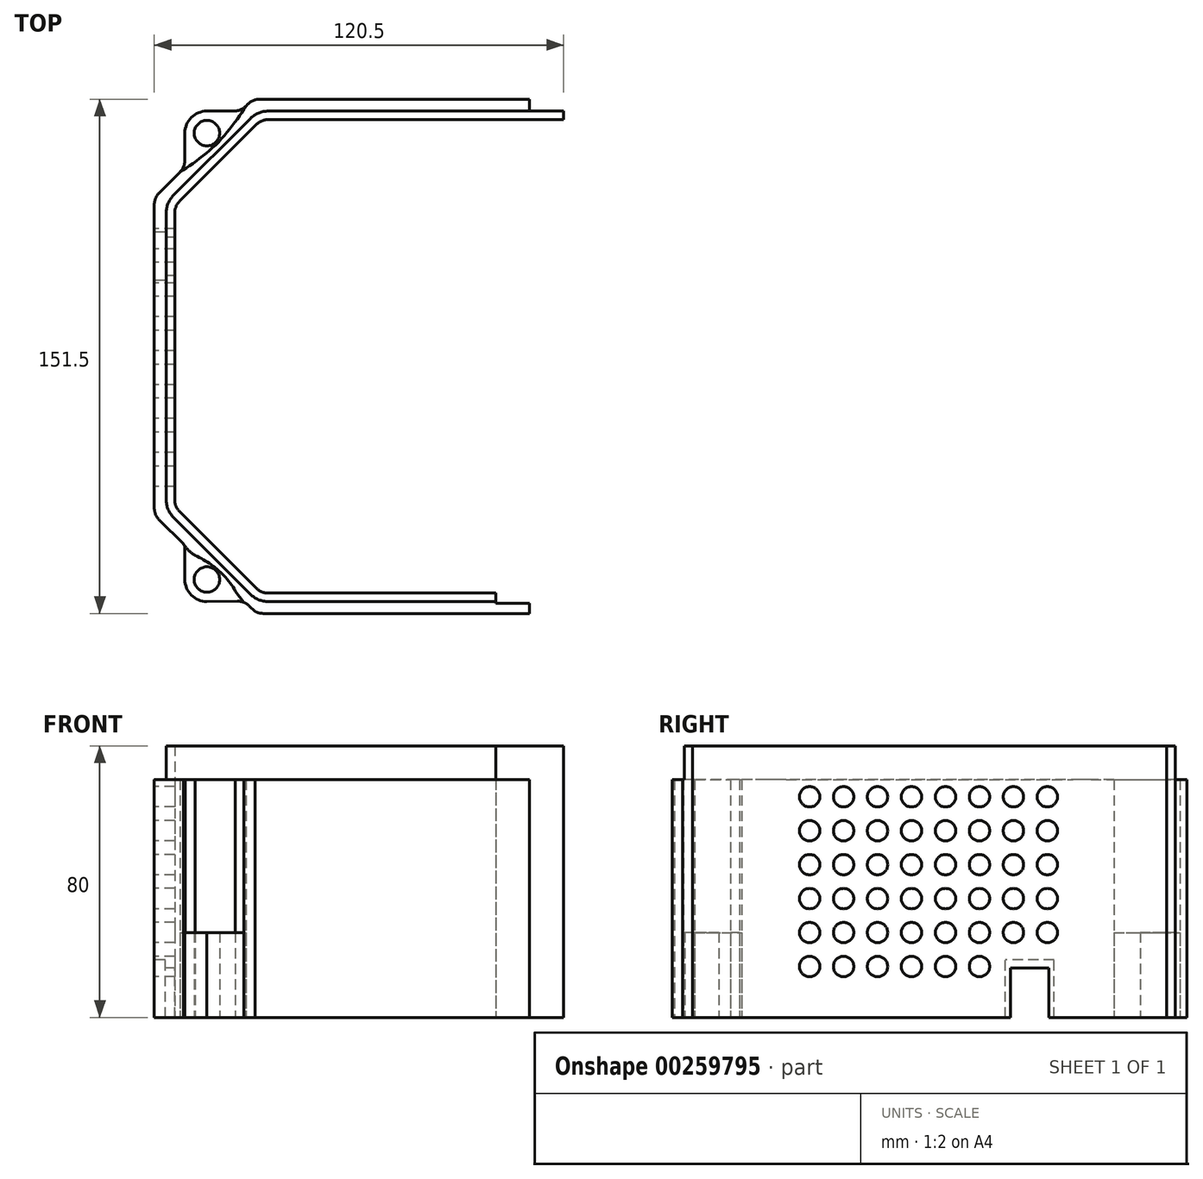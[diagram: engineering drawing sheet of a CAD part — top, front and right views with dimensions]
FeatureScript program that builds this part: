
annotation { "Feature Type Name" : "Feature", "Feature Type Description" : "" }
export const myFeature = defineFeature(function(context is Context, id is Id, definition is map)
    precondition{}
    {
        {
            var Q0;
            Q0=qCreatedBy(makeId("Top.planeOp"),FACE);
            var sketch = newSketch(context, id + "F0", { "sketchPlane" : qUnion([Q0])});
            skLineSegment(sketch, "E0.bottom", {"start": v(-49.42, 75.75) * mm, "end": v(30, 75.75) * mm});
            skLineSegment(sketch, "E0.top", {"start": v(-48.4, -75.75) * mm, "end": v(30, -75.75) * mm});
            skLineSegment(sketch, "E0.left", {"start": v(-80.5, 44.67) * mm, "end": v(-80.5, -44.67) * mm});
            skLineSegment(sketch, "E0.right", {"start": v(30, 75.75) * mm, "end": v(30, 72.25) * mm});
            skCircle(sketch, "E1", {"center": v(-65, 65.75) * mm, "radius": 3.75 * mm});
            skCircle(sketch, "E2", {"center": v(-65, -65.75) * mm, "radius": 3.75 * mm});
            skPoint(sketch, "E3.visualSharp", {"position": v(-80.5, 75.75) * mm});
            skPoint(sketch, "E4.visualSharp", {"position": v(-80.5, -75.75) * mm});
            skLineSegment(sketch, "E5.0", {"start": v(-46.93, 69.75) * mm, "end": v(30, 69.75) * mm});
            skLineSegment(sketch, "E6.trimOffspring", {"start": v(30, -72.75) * mm, "end": v(30, -75.75) * mm});
            skLineSegment(sketch, "E7", {"start": v(-73.04, 45.72) * mm, "end": v(-50.47, 68.29) * mm});
            skLineSegment(sketch, "E8", {"start": v(-73.04, -45.72) * mm, "end": v(-50.47, -68.29) * mm});
            skLineSegment(sketch, "E9.trimOffspring", {"start": v(-46.94, -69.75) * mm, "end": v(20, -69.75) * mm});
            skArc(sketch, "E10.trimOffspring", {"start": v(-60.05, -58.7) * mm, "mid": v(-60.25, -58.5) * mm, "end": v(-60.46, -58.3) * mm, "construction": true});
            skArc(sketch, "E11", {"start": v(-71.5, -65.75) * mm, "mid": v(-69.6, -70.35) * mm, "end": v(-65, -72.25) * mm});
            skArc(sketch, "E12", {"start": v(-65, 72.25) * mm, "mid": v(-69.6, 70.35) * mm, "end": v(-71.5, 65.75) * mm});
            skPoint(sketch, "E13.visualSharp", {"position": v(-49, -69.75) * mm});
            skArc(sketch, "E13.filletArc", {"start": v(-50.47, -68.29) * mm, "mid": v(-48.85, -69.37) * mm, "end": v(-46.94, -69.75) * mm});
            skPoint(sketch, "E14.visualSharp", {"position": v(-74.5, -44.26) * mm});
            skArc(sketch, "E14.filletArc", {"start": v(-74.5, -42.19) * mm, "mid": v(-74.12, -44.1) * mm, "end": v(-73.04, -45.72) * mm});
            skPoint(sketch, "E15.visualSharp", {"position": v(-74.5, 44.25) * mm});
            skArc(sketch, "E15.filletArc", {"start": v(-73.04, 45.72) * mm, "mid": v(-74.12, 44.1) * mm, "end": v(-74.5, 42.18) * mm});
            skPoint(sketch, "E16.visualSharp", {"position": v(-49, 69.75) * mm});
            skArc(sketch, "E16.filletArc", {"start": v(-46.93, 69.75) * mm, "mid": v(-48.85, 69.37) * mm, "end": v(-50.47, 68.29) * mm});
            skLineSegment(sketch, "E17", {"start": v(-79.04, -48.2) * mm, "end": v(-71.96, -55.28) * mm});
            skPoint(sketch, "E18.visualSharp", {"position": v(-70.5, -56.75) * mm});
            skArc(sketch, "E19.filletArc", {"start": v(-80.5, -44.67) * mm, "mid": v(-80.12, -46.59) * mm, "end": v(-79.04, -48.2) * mm});
            skPoint(sketch, "E20.visualSharp", {"position": v(-56, -71.25) * mm});
            skPoint(sketch, "E21.visualSharp", {"position": v(-51.5, -75.75) * mm});
            skArc(sketch, "E21.filletArc", {"start": v(-50.86, -75.1) * mm, "mid": v(-49.68, -75.59) * mm, "end": v(-48.4, -75.75) * mm});
            skLineSegment(sketch, "E22", {"start": v(-65, 72.25) * mm, "end": v(-57.06, 72.25) * mm});
            skLineSegment(sketch, "E23", {"start": v(-71.5, 57.81) * mm, "end": v(-71.5, 65.75) * mm});
            skLineSegment(sketch, "E24", {"start": v(-72.96, 54.28) * mm, "end": v(-79.04, 48.2) * mm});
            skLineSegment(sketch, "E25", {"start": v(-53.53, 73.71) * mm, "end": v(-52.95, 74.29) * mm});
            skPoint(sketch, "E26.visualSharp", {"position": v(-80.5, 46.74) * mm});
            skArc(sketch, "E26.filletArc", {"start": v(-79.04, 48.2) * mm, "mid": v(-80.12, 46.58) * mm, "end": v(-80.5, 44.67) * mm});
            skPoint(sketch, "E27.visualSharp", {"position": v(-71.5, 55.74) * mm});
            skArc(sketch, "E27.filletArc", {"start": v(-72.96, 54.28) * mm, "mid": v(-71.88, 55.9) * mm, "end": v(-71.5, 57.81) * mm});
            skPoint(sketch, "E28.visualSharp", {"position": v(-54.99, 72.25) * mm});
            skArc(sketch, "E28.filletArc", {"start": v(-57.06, 72.25) * mm, "mid": v(-55.15, 72.63) * mm, "end": v(-53.53, 73.71) * mm});
            skPoint(sketch, "E29.visualSharp", {"position": v(-51.49, 75.75) * mm});
            skArc(sketch, "E29.filletArc", {"start": v(-49.42, 75.75) * mm, "mid": v(-51.33, 75.37) * mm, "end": v(-52.95, 74.29) * mm});
            skLineSegment(sketch, "E30", {"start": v(-74.5, -42.19) * mm, "end": v(-74.5, 42.18) * mm});
            skLineSegment(sketch, "E31", {"start": v(-59, -59.75) * mm, "end": v(-80.03, -80.78) * mm, "construction": true});
            skArc(sketch, "E32.filletArc", {"start": v(-71.36, -56.02) * mm, "mid": v(-70.06, -57.5) * mm, "end": v(-68.44, -58.62) * mm});
            skPoint(sketch, "E33.orphan", {"position": v(-62.35, -63.1) * mm});
            skPoint(sketch, "E34.orphan", {"position": v(-56, -69.45) * mm});
            skPoint(sketch, "E35.orphan", {"position": v(-68.7, -56.75) * mm});
            skPoint(sketch, "E36", {"position": v(-62, -62.74) * mm});
            skFitSpline(sketch, "E37", {"points": [v(-56.66, -69.17) * mm, v(-62, -62.74) * mm, v(-68.44, -58.62) * mm], "startDerivative": vector(-7.08, 14.05) * mm, "endDerivative": vector(-14.05, 7.08) * mm});
            skLineSegment(sketch, "E38", {"start": v(-62, 62.74) * mm, "end": v(-62.35, 63.1) * mm, "construction": true});
            skPoint(sketch, "E39", {"position": v(-62, 62.74) * mm});
            skFitSpline(sketch, "E40", {"points": [v(-72.96, 54.28) * mm, v(-62, 62.74) * mm, v(-53.53, 73.71) * mm], "startDerivative": vector(21.19, 13.69) * mm, "endDerivative": vector(13.69, 21.19) * mm});
            skLineSegment(sketch, "E41.trimOffspring", {"start": v(-67.65, 68.4) * mm, "end": v(-69.6, 70.35) * mm, "construction": true});
            skLineSegment(sketch, "E42", {"start": v(-71.97, -55.28) * mm, "end": v(-71.96, -55.28) * mm});
            skLineSegment(sketch, "E43", {"start": v(-71.5, -65.75) * mm, "end": v(-71.5, -56.56) * mm});
            skLineSegment(sketch, "E44", {"start": v(-65, -72.25) * mm, "end": v(-56.04, -72.14) * mm});
            skArc(sketch, "E45.filletArc", {"start": v(-71.5, -56.56) * mm, "mid": v(-71.62, -55.88) * mm, "end": v(-71.97, -55.28) * mm});
            skLineSegment(sketch, "E46", {"start": v(-50.86, -75.1) * mm, "end": v(-52.55, -73.51) * mm});
            skPoint(sketch, "E47.visualSharp", {"position": v(-54.02, -72.12) * mm});
            skArc(sketch, "E47.filletArc", {"start": v(-52.55, -73.51) * mm, "mid": v(-54.16, -72.49) * mm, "end": v(-56.04, -72.14) * mm});
            skLineSegment(sketch, "E48", {"start": v(-56.66, -69.17) * mm, "end": v(-54.16, -72.49) * mm});
            skLineSegment(sketch, "E49", {"start": v(-71.36, -56.02) * mm, "end": v(-71.96, -55.28) * mm});
            skLineSegment(sketch, "E50.bottom", {"start": v(30, 69.75) * mm, "end": v(40, 69.75) * mm});
            skLineSegment(sketch, "E50.top", {"start": v(30, 72.25) * mm, "end": v(40, 72.25) * mm});
            skLineSegment(sketch, "E50.right", {"start": v(40, 69.75) * mm, "end": v(40, 72.25) * mm});
            skLineSegment(sketch, "E51.top", {"start": v(20, -72.75) * mm, "end": v(30, -72.75) * mm});
            skLineSegment(sketch, "E51.left", {"start": v(20, -69.75) * mm, "end": v(20, -72.75) * mm});
            skSolve(sketch);
        }
        {
            var Q0;
            Q0=makeQuery(id+"F0.imprint","IMPRINT",FACE,{"disambiguationData":[TD([[makeQuery(id+"F0.imprint","IMPRINT",EDGE,{"derivedFrom":sQuery(id+"F0.wireOp",EDGE,"E2")}),-1.0]])]});
            var Q1;
            Q1=makeQuery(id+"F0.imprint","IMPRINT",FACE,{"disambiguationData":[TD([[makeQuery(id+"F0.imprint","IMPRINT",EDGE,{"derivedFrom":sQuery(id+"F0.wireOp",EDGE,"E1")}),-1.0]])]});
            extrude(context, id + "F1", {"entities" : qUnion([Q0, Q1]), "depth" : 25 * mm});
        }
        {
            var Q0;
            Q0=makeQuery(id+"F0.imprint","IMPRINT",FACE,{"disambiguationData":[TD([[makeQuery(id+"F0.imprint","IMPRINT",EDGE,{"derivedFrom":sQuery(id+"F0.wireOp",EDGE,"E0.bottom")}),-1.0]])]});
            extrude(context, id + "F2", {"entities" : qUnion([Q0]), "depth" : 70 * mm});
        }
        {
            var Q0;
            Q0=makeQuery(id+"F2.opExtrude","CAP_FACE",FACE,{"disambiguationData":[OSD([sQuery(id+"F0.wireOp",EDGE,"E0.bottom"),sQuery(id+"F0.wireOp",EDGE,"E0.top"),sQuery(id+"F0.wireOp",EDGE,"E0.left"),sQuery(id+"F0.wireOp",EDGE,"E0.right"),sQuery(id+"F0.wireOp",EDGE,"E5.0"),sQuery(id+"F0.wireOp",EDGE,"E6.trimOffspring"),sQuery(id+"F0.wireOp",EDGE,"E7"),sQuery(id+"F0.wireOp",EDGE,"E8"),sQuery(id+"F0.wireOp",EDGE,"E9.trimOffspring"),sQuery(id+"F0.wireOp",EDGE,"E13.filletArc"),sQuery(id+"F0.wireOp",EDGE,"E14.filletArc"),sQuery(id+"F0.wireOp",EDGE,"E15.filletArc"),sQuery(id+"F0.wireOp",EDGE,"E16.filletArc"),sQuery(id+"F0.wireOp",EDGE,"E17"),sQuery(id+"F0.wireOp",EDGE,"E19.filletArc"),sQuery(id+"F0.wireOp",EDGE,"E21.filletArc"),sQuery(id+"F0.wireOp",EDGE,"E24"),sQuery(id+"F0.wireOp",EDGE,"E25"),sQuery(id+"F0.wireOp",EDGE,"E26.filletArc"),sQuery(id+"F0.wireOp",EDGE,"E29.filletArc"),sQuery(id+"F0.wireOp",EDGE,"E30"),sQuery(id+"F0.wireOp",EDGE,"E32.filletArc"),sQuery(id+"F0.wireOp",EDGE,"E37"),sQuery(id+"F0.wireOp",EDGE,"E40"),sQuery(id+"F0.wireOp",EDGE,"E46"),sQuery(id+"F0.wireOp",EDGE,"E47.filletArc"),sQuery(id+"F0.wireOp",EDGE,"E48"),sQuery(id+"F0.wireOp",EDGE,"E49"),sQuery(id+"F0.wireOp",EDGE,"E50.bottom"),sQuery(id+"F0.wireOp",EDGE,"E50.top"),sQuery(id+"F0.wireOp",EDGE,"E50.right"),sQuery(id+"F0.wireOp",EDGE,"E51.top"),sQuery(id+"F0.wireOp",EDGE,"E51.left")])],"isStart":false});
            var sketch = newSketch(context, id + "F3", { "sketchPlane" : qUnion([Q0])});
            skLineSegment(sketch, "E52.0", {"start": v(-46.94, -72.25) * mm, "end": v(20, -72.25) * mm});
            skArc(sketch, "E52.1", {"start": v(-52.24, -70.05) * mm, "mid": v(-49.8, -71.68) * mm, "end": v(-46.94, -72.25) * mm});
            skLineSegment(sketch, "E52.2", {"start": v(-74.8, -47.5) * mm, "end": v(-52.24, -70.05) * mm});
            skArc(sketch, "E52.3", {"start": v(-77, -42.19) * mm, "mid": v(-76.43, -45.06) * mm, "end": v(-74.8, -47.5) * mm});
            skLineSegment(sketch, "E52.4", {"start": v(-77, -42.19) * mm, "end": v(-77, 42.18) * mm});
            skArc(sketch, "E52.5", {"start": v(-74.8, 47.49) * mm, "mid": v(-76.43, 45.05) * mm, "end": v(-77, 42.18) * mm});
            skLineSegment(sketch, "E52.6", {"start": v(30, 72.25) * mm, "end": v(40, 72.25) * mm});
            skLineSegment(sketch, "E52.7", {"start": v(-46.93, 72.25) * mm, "end": v(30, 72.25) * mm});
            skArc(sketch, "E52.8", {"start": v(-46.93, 72.25) * mm, "mid": v(-49.8, 71.68) * mm, "end": v(-52.24, 70.05) * mm});
            skLineSegment(sketch, "E52.9", {"start": v(-74.8, 47.49) * mm, "end": v(-52.24, 70.05) * mm});
            skLineSegment(sketch, "E53", {"start": v(20, -72.25) * mm, "end": v(20, -69.75) * mm});
            skLineSegment(sketch, "E54", {"start": v(40, 69.75) * mm, "end": v(40, 72.25) * mm});
            skSolve(sketch);
        }
        {
            var Q0;
            Q0=makeQuery(id+"F3.imprint","IMPRINT",FACE,{"disambiguationData":[TD([[makeQuery(id+"F3.imprint","IMPRINT",EDGE,{"derivedFrom":sQuery(id+"F3.wireOp",EDGE,"E52.0")}),1.0]])]});
            extrude(context, id + "F4", {"entities" : qUnion([Q0]), "operationType" : NewBodyOperationType.ADD, "depth" : 10 * mm});
        }
        {
            var Q0;
            Q0=makeQuery(id+"F2.opExtrude","SWEPT_FACE",FACE,{"disambiguationData":[OSD([sQuery(id+"F0.wireOp",EDGE,"E0.left")])]});
            var sketch = newSketch(context, id + "F5", { "sketchPlane" : qUnion([Q0])});
            skCircle(sketch, "E55.0.1.0", {"center": v(-34.67, 25) * mm, "radius": 3 * mm});
            skCircle(sketch, "E55.0.2.0", {"center": v(-34.67, 35) * mm, "radius": 3 * mm});
            skCircle(sketch, "E55.0.3.0", {"center": v(-34.67, 45) * mm, "radius": 3 * mm});
            skCircle(sketch, "E55.0.4.0", {"center": v(-34.67, 55) * mm, "radius": 3 * mm});
            skCircle(sketch, "E55.0.5.0", {"center": v(-34.67, 65) * mm, "radius": 3 * mm});
            skCircle(sketch, "E55.1.1.0", {"center": v(-24.67, 25) * mm, "radius": 3 * mm});
            skCircle(sketch, "E55.1.2.0", {"center": v(-24.67, 35) * mm, "radius": 3 * mm});
            skCircle(sketch, "E55.1.3.0", {"center": v(-24.67, 45) * mm, "radius": 3 * mm});
            skCircle(sketch, "E55.1.4.0", {"center": v(-24.67, 55) * mm, "radius": 3 * mm});
            skCircle(sketch, "E55.1.5.0", {"center": v(-24.67, 65) * mm, "radius": 3 * mm});
            skCircle(sketch, "E55.2.0.0", {"center": v(-14.67, 15) * mm, "radius": 3 * mm});
            skCircle(sketch, "E55.2.1.0", {"center": v(-14.67, 25) * mm, "radius": 3 * mm});
            skCircle(sketch, "E55.2.2.0", {"center": v(-14.67, 35) * mm, "radius": 3 * mm});
            skCircle(sketch, "E55.2.3.0", {"center": v(-14.67, 45) * mm, "radius": 3 * mm});
            skCircle(sketch, "E55.2.4.0", {"center": v(-14.67, 55) * mm, "radius": 3 * mm});
            skCircle(sketch, "E55.2.5.0", {"center": v(-14.67, 65) * mm, "radius": 3 * mm});
            skCircle(sketch, "E55.3.0.0", {"center": v(-4.67, 15) * mm, "radius": 3 * mm});
            skCircle(sketch, "E55.3.1.0", {"center": v(-4.67, 25) * mm, "radius": 3 * mm});
            skCircle(sketch, "E55.3.2.0", {"center": v(-4.67, 35) * mm, "radius": 3 * mm});
            skCircle(sketch, "E55.3.3.0", {"center": v(-4.67, 45) * mm, "radius": 3 * mm});
            skCircle(sketch, "E55.3.4.0", {"center": v(-4.67, 55) * mm, "radius": 3 * mm});
            skCircle(sketch, "E55.3.5.0", {"center": v(-4.67, 65) * mm, "radius": 3 * mm});
            skCircle(sketch, "E55.4.0.0", {"center": v(5.33, 15) * mm, "radius": 3 * mm});
            skCircle(sketch, "E55.4.1.0", {"center": v(5.33, 25) * mm, "radius": 3 * mm});
            skCircle(sketch, "E55.4.2.0", {"center": v(5.33, 35) * mm, "radius": 3 * mm});
            skCircle(sketch, "E55.4.3.0", {"center": v(5.33, 45) * mm, "radius": 3 * mm});
            skCircle(sketch, "E55.4.4.0", {"center": v(5.33, 55) * mm, "radius": 3 * mm});
            skCircle(sketch, "E55.4.5.0", {"center": v(5.33, 65) * mm, "radius": 3 * mm});
            skCircle(sketch, "E55.5.0.0", {"center": v(15.33, 15) * mm, "radius": 3 * mm});
            skCircle(sketch, "E55.5.1.0", {"center": v(15.33, 25) * mm, "radius": 3 * mm});
            skCircle(sketch, "E55.5.2.0", {"center": v(15.33, 35) * mm, "radius": 3 * mm});
            skCircle(sketch, "E55.5.3.0", {"center": v(15.33, 45) * mm, "radius": 3 * mm});
            skCircle(sketch, "E55.5.4.0", {"center": v(15.33, 55) * mm, "radius": 3 * mm});
            skCircle(sketch, "E55.5.5.0", {"center": v(15.33, 65) * mm, "radius": 3 * mm});
            skCircle(sketch, "E55.6.0.0", {"center": v(25.33, 15) * mm, "radius": 3 * mm});
            skCircle(sketch, "E55.6.1.0", {"center": v(25.33, 25) * mm, "radius": 3 * mm});
            skCircle(sketch, "E55.6.2.0", {"center": v(25.33, 35) * mm, "radius": 3 * mm});
            skCircle(sketch, "E55.6.3.0", {"center": v(25.33, 45) * mm, "radius": 3 * mm});
            skCircle(sketch, "E55.6.4.0", {"center": v(25.33, 55) * mm, "radius": 3 * mm});
            skCircle(sketch, "E55.6.5.0", {"center": v(25.33, 65) * mm, "radius": 3 * mm});
            skCircle(sketch, "E55.7.0.0", {"center": v(35.33, 15) * mm, "radius": 3 * mm});
            skCircle(sketch, "E55.7.1.0", {"center": v(35.33, 25) * mm, "radius": 3 * mm});
            skCircle(sketch, "E55.7.2.0", {"center": v(35.33, 35) * mm, "radius": 3 * mm});
            skCircle(sketch, "E55.7.3.0", {"center": v(35.33, 45) * mm, "radius": 3 * mm});
            skCircle(sketch, "E55.7.4.0", {"center": v(35.33, 55) * mm, "radius": 3 * mm});
            skCircle(sketch, "E55.7.5.0", {"center": v(35.33, 65) * mm, "radius": 3 * mm});
            skLineSegment(sketch, "E55.direction1", {"start": v(-34.67, 15) * mm, "end": v(-24.67, 15) * mm, "construction": true});
            skLineSegment(sketch, "E55.direction2", {"start": v(-34.67, 15) * mm, "end": v(-34.67, 25) * mm, "construction": true});
            skSolve(sketch);
        }
        {
            var Q0;
            Q0=makeQuery(id+"F5.imprint","IMPRINT",FACE,{"disambiguationData":[TD([[makeQuery(id+"F5.imprint","IMPRINT",EDGE,{"derivedFrom":sQuery(id+"F5.wireOp",EDGE,"E55.1.5.0")}),1.0]])]});
            var Q1;
            Q1=makeQuery(id+"F5.imprint","IMPRINT",FACE,{"disambiguationData":[TD([[makeQuery(id+"F5.imprint","IMPRINT",EDGE,{"derivedFrom":sQuery(id+"F5.wireOp",EDGE,"E55.0.5.0")}),1.0]])]});
            var Q2;
            Q2=makeQuery(id+"F5.imprint","IMPRINT",FACE,{"disambiguationData":[TD([[makeQuery(id+"F5.imprint","IMPRINT",EDGE,{"derivedFrom":sQuery(id+"F5.wireOp",EDGE,"E55.2.5.0")}),1.0]])]});
            var Q3;
            Q3=makeQuery(id+"F5.imprint","IMPRINT",FACE,{"disambiguationData":[TD([[makeQuery(id+"F5.imprint","IMPRINT",EDGE,{"derivedFrom":sQuery(id+"F5.wireOp",EDGE,"E55.3.5.0")}),1.0]])]});
            var Q4;
            Q4=makeQuery(id+"F5.imprint","IMPRINT",FACE,{"disambiguationData":[TD([[makeQuery(id+"F5.imprint","IMPRINT",EDGE,{"derivedFrom":sQuery(id+"F5.wireOp",EDGE,"E55.4.5.0")}),1.0]])]});
            var Q5;
            Q5=makeQuery(id+"F5.imprint","IMPRINT",FACE,{"disambiguationData":[TD([[makeQuery(id+"F5.imprint","IMPRINT",EDGE,{"derivedFrom":sQuery(id+"F5.wireOp",EDGE,"E55.5.5.0")}),1.0]])]});
            var Q6;
            Q6=makeQuery(id+"F5.imprint","IMPRINT",FACE,{"disambiguationData":[TD([[makeQuery(id+"F5.imprint","IMPRINT",EDGE,{"derivedFrom":sQuery(id+"F5.wireOp",EDGE,"E55.6.5.0")}),1.0]])]});
            var Q7;
            Q7=makeQuery(id+"F5.imprint","IMPRINT",FACE,{"disambiguationData":[TD([[makeQuery(id+"F5.imprint","IMPRINT",EDGE,{"derivedFrom":sQuery(id+"F5.wireOp",EDGE,"E55.7.5.0")}),1.0]])]});
            var Q8;
            Q8=makeQuery(id+"F5.imprint","IMPRINT",FACE,{"disambiguationData":[TD([[makeQuery(id+"F5.imprint","IMPRINT",EDGE,{"derivedFrom":sQuery(id+"F5.wireOp",EDGE,"E55.7.4.0")}),1.0]])]});
            var Q9;
            Q9=makeQuery(id+"F5.imprint","IMPRINT",FACE,{"disambiguationData":[TD([[makeQuery(id+"F5.imprint","IMPRINT",EDGE,{"derivedFrom":sQuery(id+"F5.wireOp",EDGE,"E55.6.4.0")}),1.0]])]});
            var Q10;
            Q10=makeQuery(id+"F5.imprint","IMPRINT",FACE,{"disambiguationData":[TD([[makeQuery(id+"F5.imprint","IMPRINT",EDGE,{"derivedFrom":sQuery(id+"F5.wireOp",EDGE,"E55.5.4.0")}),1.0]])]});
            var Q11;
            Q11=makeQuery(id+"F5.imprint","IMPRINT",FACE,{"disambiguationData":[TD([[makeQuery(id+"F5.imprint","IMPRINT",EDGE,{"derivedFrom":sQuery(id+"F5.wireOp",EDGE,"E55.4.4.0")}),1.0]])]});
            var Q12;
            Q12=makeQuery(id+"F5.imprint","IMPRINT",FACE,{"disambiguationData":[TD([[makeQuery(id+"F5.imprint","IMPRINT",EDGE,{"derivedFrom":sQuery(id+"F5.wireOp",EDGE,"E55.3.4.0")}),1.0]])]});
            var Q13;
            Q13=makeQuery(id+"F5.imprint","IMPRINT",FACE,{"disambiguationData":[TD([[makeQuery(id+"F5.imprint","IMPRINT",EDGE,{"derivedFrom":sQuery(id+"F5.wireOp",EDGE,"E55.2.4.0")}),1.0]])]});
            var Q14;
            Q14=makeQuery(id+"F5.imprint","IMPRINT",FACE,{"disambiguationData":[TD([[makeQuery(id+"F5.imprint","IMPRINT",EDGE,{"derivedFrom":sQuery(id+"F5.wireOp",EDGE,"E55.1.4.0")}),1.0]])]});
            var Q15;
            Q15=makeQuery(id+"F5.imprint","IMPRINT",FACE,{"disambiguationData":[TD([[makeQuery(id+"F5.imprint","IMPRINT",EDGE,{"derivedFrom":sQuery(id+"F5.wireOp",EDGE,"E55.0.4.0")}),1.0]])]});
            var Q16;
            Q16=makeQuery(id+"F5.imprint","IMPRINT",FACE,{"disambiguationData":[TD([[makeQuery(id+"F5.imprint","IMPRINT",EDGE,{"derivedFrom":sQuery(id+"F5.wireOp",EDGE,"E55.0.3.0")}),1.0]])]});
            var Q17;
            Q17=makeQuery(id+"F5.imprint","IMPRINT",FACE,{"disambiguationData":[TD([[makeQuery(id+"F5.imprint","IMPRINT",EDGE,{"derivedFrom":sQuery(id+"F5.wireOp",EDGE,"E55.1.3.0")}),1.0]])]});
            var Q18;
            Q18=makeQuery(id+"F5.imprint","IMPRINT",FACE,{"disambiguationData":[TD([[makeQuery(id+"F5.imprint","IMPRINT",EDGE,{"derivedFrom":sQuery(id+"F5.wireOp",EDGE,"E55.2.3.0")}),1.0]])]});
            var Q19;
            Q19=makeQuery(id+"F5.imprint","IMPRINT",FACE,{"disambiguationData":[TD([[makeQuery(id+"F5.imprint","IMPRINT",EDGE,{"derivedFrom":sQuery(id+"F5.wireOp",EDGE,"E55.3.3.0")}),1.0]])]});
            var Q20;
            Q20=makeQuery(id+"F5.imprint","IMPRINT",FACE,{"disambiguationData":[TD([[makeQuery(id+"F5.imprint","IMPRINT",EDGE,{"derivedFrom":sQuery(id+"F5.wireOp",EDGE,"E55.4.3.0")}),1.0]])]});
            var Q21;
            Q21=makeQuery(id+"F5.imprint","IMPRINT",FACE,{"disambiguationData":[TD([[makeQuery(id+"F5.imprint","IMPRINT",EDGE,{"derivedFrom":sQuery(id+"F5.wireOp",EDGE,"E55.5.3.0")}),1.0]])]});
            var Q22;
            Q22=makeQuery(id+"F5.imprint","IMPRINT",FACE,{"disambiguationData":[TD([[makeQuery(id+"F5.imprint","IMPRINT",EDGE,{"derivedFrom":sQuery(id+"F5.wireOp",EDGE,"E55.6.3.0")}),1.0]])]});
            var Q23;
            Q23=makeQuery(id+"F5.imprint","IMPRINT",FACE,{"disambiguationData":[TD([[makeQuery(id+"F5.imprint","IMPRINT",EDGE,{"derivedFrom":sQuery(id+"F5.wireOp",EDGE,"E55.7.3.0")}),1.0]])]});
            var Q24;
            Q24=makeQuery(id+"F5.imprint","IMPRINT",FACE,{"disambiguationData":[TD([[makeQuery(id+"F5.imprint","IMPRINT",EDGE,{"derivedFrom":sQuery(id+"F5.wireOp",EDGE,"E55.7.2.0")}),1.0]])]});
            var Q25;
            Q25=makeQuery(id+"F5.imprint","IMPRINT",FACE,{"disambiguationData":[TD([[makeQuery(id+"F5.imprint","IMPRINT",EDGE,{"derivedFrom":sQuery(id+"F5.wireOp",EDGE,"E55.6.2.0")}),1.0]])]});
            var Q26;
            Q26=makeQuery(id+"F5.imprint","IMPRINT",FACE,{"disambiguationData":[TD([[makeQuery(id+"F5.imprint","IMPRINT",EDGE,{"derivedFrom":sQuery(id+"F5.wireOp",EDGE,"E55.5.2.0")}),1.0]])]});
            var Q27;
            Q27=makeQuery(id+"F5.imprint","IMPRINT",FACE,{"disambiguationData":[TD([[makeQuery(id+"F5.imprint","IMPRINT",EDGE,{"derivedFrom":sQuery(id+"F5.wireOp",EDGE,"E55.4.2.0")}),1.0]])]});
            var Q28;
            Q28=makeQuery(id+"F5.imprint","IMPRINT",FACE,{"disambiguationData":[TD([[makeQuery(id+"F5.imprint","IMPRINT",EDGE,{"derivedFrom":sQuery(id+"F5.wireOp",EDGE,"E55.3.2.0")}),1.0]])]});
            var Q29;
            Q29=makeQuery(id+"F5.imprint","IMPRINT",FACE,{"disambiguationData":[TD([[makeQuery(id+"F5.imprint","IMPRINT",EDGE,{"derivedFrom":sQuery(id+"F5.wireOp",EDGE,"E55.2.2.0")}),1.0]])]});
            var Q30;
            Q30=makeQuery(id+"F5.imprint","IMPRINT",FACE,{"disambiguationData":[TD([[makeQuery(id+"F5.imprint","IMPRINT",EDGE,{"derivedFrom":sQuery(id+"F5.wireOp",EDGE,"E55.1.2.0")}),1.0]])]});
            var Q31;
            Q31=makeQuery(id+"F5.imprint","IMPRINT",FACE,{"disambiguationData":[TD([[makeQuery(id+"F5.imprint","IMPRINT",EDGE,{"derivedFrom":sQuery(id+"F5.wireOp",EDGE,"E55.0.2.0")}),1.0]])]});
            var Q32;
            Q32=makeQuery(id+"F5.imprint","IMPRINT",FACE,{"disambiguationData":[TD([[makeQuery(id+"F5.imprint","IMPRINT",EDGE,{"derivedFrom":sQuery(id+"F5.wireOp",EDGE,"E55.0.1.0")}),1.0]])]});
            var Q33;
            Q33=makeQuery(id+"F5.imprint","IMPRINT",FACE,{"disambiguationData":[TD([[makeQuery(id+"F5.imprint","IMPRINT",EDGE,{"derivedFrom":sQuery(id+"F5.wireOp",EDGE,"E55.1.1.0")}),1.0]])]});
            var Q34;
            Q34=makeQuery(id+"F5.imprint","IMPRINT",FACE,{"disambiguationData":[TD([[makeQuery(id+"F5.imprint","IMPRINT",EDGE,{"derivedFrom":sQuery(id+"F5.wireOp",EDGE,"E55.2.1.0")}),1.0]])]});
            var Q35;
            Q35=makeQuery(id+"F5.imprint","IMPRINT",FACE,{"disambiguationData":[TD([[makeQuery(id+"F5.imprint","IMPRINT",EDGE,{"derivedFrom":sQuery(id+"F5.wireOp",EDGE,"E55.3.1.0")}),1.0]])]});
            var Q36;
            Q36=makeQuery(id+"F5.imprint","IMPRINT",FACE,{"disambiguationData":[TD([[makeQuery(id+"F5.imprint","IMPRINT",EDGE,{"derivedFrom":sQuery(id+"F5.wireOp",EDGE,"E55.4.1.0")}),1.0]])]});
            var Q37;
            Q37=makeQuery(id+"F5.imprint","IMPRINT",FACE,{"disambiguationData":[TD([[makeQuery(id+"F5.imprint","IMPRINT",EDGE,{"derivedFrom":sQuery(id+"F5.wireOp",EDGE,"E55.5.1.0")}),1.0]])]});
            var Q38;
            Q38=makeQuery(id+"F5.imprint","IMPRINT",FACE,{"disambiguationData":[TD([[makeQuery(id+"F5.imprint","IMPRINT",EDGE,{"derivedFrom":sQuery(id+"F5.wireOp",EDGE,"E55.6.1.0")}),1.0]])]});
            var Q39;
            Q39=makeQuery(id+"F5.imprint","IMPRINT",FACE,{"disambiguationData":[TD([[makeQuery(id+"F5.imprint","IMPRINT",EDGE,{"derivedFrom":sQuery(id+"F5.wireOp",EDGE,"E55.7.1.0")}),1.0]])]});
            var Q40;
            Q40=makeQuery(id+"F5.imprint","IMPRINT",FACE,{"disambiguationData":[TD([[makeQuery(id+"F5.imprint","IMPRINT",EDGE,{"derivedFrom":sQuery(id+"F5.wireOp",EDGE,"E55.7.0.0")}),1.0]])]});
            var Q41;
            Q41=makeQuery(id+"F5.imprint","IMPRINT",FACE,{"disambiguationData":[TD([[makeQuery(id+"F5.imprint","IMPRINT",EDGE,{"derivedFrom":sQuery(id+"F5.wireOp",EDGE,"E55.6.0.0")}),1.0]])]});
            var Q42;
            Q42=makeQuery(id+"F5.imprint","IMPRINT",FACE,{"disambiguationData":[TD([[makeQuery(id+"F5.imprint","IMPRINT",EDGE,{"derivedFrom":sQuery(id+"F5.wireOp",EDGE,"E55.5.0.0")}),1.0]])]});
            var Q43;
            Q43=makeQuery(id+"F5.imprint","IMPRINT",FACE,{"disambiguationData":[TD([[makeQuery(id+"F5.imprint","IMPRINT",EDGE,{"derivedFrom":sQuery(id+"F5.wireOp",EDGE,"E55.4.0.0")}),1.0]])]});
            var Q44;
            Q44=makeQuery(id+"F5.imprint","IMPRINT",FACE,{"disambiguationData":[TD([[makeQuery(id+"F5.imprint","IMPRINT",EDGE,{"derivedFrom":sQuery(id+"F5.wireOp",EDGE,"E55.3.0.0")}),1.0]])]});
            var Q45;
            Q45=makeQuery(id+"F5.imprint","IMPRINT",FACE,{"disambiguationData":[TD([[makeQuery(id+"F5.imprint","IMPRINT",EDGE,{"derivedFrom":sQuery(id+"F5.wireOp",EDGE,"E55.2.0.0")}),1.0]])]});
            var Q46;
            Q46=makeQuery(id+"F5.imprint","IMPRINT",FACE,{"disambiguationData":[TD([[makeQuery(id+"F5.imprint","IMPRINT",EDGE,{"derivedFrom":sQuery(id+"F5.wireOp",EDGE,"E55.1.0.0")}),1.0]])]});
            var Q47;
            Q47=makeQuery(id+"F5.imprint","IMPRINT",FACE,{"disambiguationData":[TD([[makeQuery(id+"F5.imprint","IMPRINT",EDGE,{"derivedFrom":sQuery(id+"F5.wireOp",EDGE,"HXi4QBqs-lh6d-TIMB-6jUE-6eJl1C0j7P9a")}),1.0]])]});
            extrude(context, id + "F6", {"entities" : qUnion([Q0, Q1, Q2, Q3, Q4, Q5, Q6, Q7, Q8, Q9, Q10, Q11, Q12, Q13, Q14, Q15, Q16, Q17, Q18, Q19, Q20, Q21, Q22, Q23, Q24, Q25, Q26, Q27, Q28, Q29, Q30, Q31, Q32, Q33, Q34, Q35, Q36, Q37, Q38, Q39, Q40, Q41, Q42, Q43, Q44, Q45, Q46, Q47]), "operationType" : NewBodyOperationType.REMOVE, "oppositeDirection" : true, "depth" : 25 * mm});
        }
        {
            var Q0;
            Q0=makeQuery(id+"F2.opExtrude","SWEPT_FACE",FACE,{"disambiguationData":[OSD([sQuery(id+"F0.wireOp",EDGE,"E0.left")])]});
            var sketch = newSketch(context, id + "F7", { "sketchPlane" : qUnion([Q0])});
            skLineSegment(sketch, "E56.bottom", {"start": v(-35.13, 0) * mm, "end": v(-23.83, 0) * mm});
            skLineSegment(sketch, "E56.top", {"start": v(-35.13, 14.5) * mm, "end": v(-23.83, 14.5) * mm});
            skLineSegment(sketch, "E56.left", {"start": v(-35.13, 0) * mm, "end": v(-35.13, 14.5) * mm});
            skLineSegment(sketch, "E56.right", {"start": v(-23.83, 0) * mm, "end": v(-23.83, 14.5) * mm});
            skLineSegment(sketch, "E57.bottom", {"start": v(-36.63, 0) * mm, "end": v(-22.33, 0) * mm});
            skLineSegment(sketch, "E57.top", {"start": v(-36.63, 17) * mm, "end": v(-22.33, 17) * mm});
            skLineSegment(sketch, "E57.left", {"start": v(-36.63, 0) * mm, "end": v(-36.63, 17) * mm});
            skLineSegment(sketch, "E57.right", {"start": v(-22.33, 0) * mm, "end": v(-22.33, 17) * mm});
            skSolve(sketch);
        }
        {
            var Q0;
            Q0=makeQuery(id+"F7.imprint","IMPRINT",FACE,{"disambiguationData":[TD([[makeQuery(id+"F7.imprint","IMPRINT",EDGE,{"derivedFrom":sQuery(id+"F7.wireOp",EDGE,"E56.top")}),-1.0]])]});
            extrude(context, id + "F8", {"entities" : qUnion([Q0]), "operationType" : NewBodyOperationType.REMOVE, "oppositeDirection" : true, "depth" : 25 * mm});
        }
        {
            var Q0;
            Q0=makeQuery(id+"F7.imprint","IMPRINT",FACE,{"disambiguationData":[TD([[makeQuery(id+"F7.imprint","IMPRINT",EDGE,{"derivedFrom":sQuery(id+"F7.wireOp",EDGE,"E56.top")}),1.0]])]});
            extrude(context, id + "F9", {"entities" : qUnion([Q0]), "operationType" : NewBodyOperationType.REMOVE, "oppositeDirection" : true, "depth" : 3.25 * mm});
        }
    });
